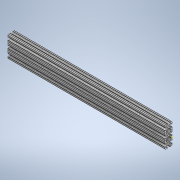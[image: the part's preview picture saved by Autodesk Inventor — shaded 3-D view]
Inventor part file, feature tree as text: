
AUTODESK INVENTOR PART (.ipt)
format: ipt  version: 2020 (Build 240168000, 168)  size: 379,904 bytes
history: native  units: in
note: dims shown in document units (in); Inventor stores cm internally (conversion verified against a paired STEP export)
features: sketch x2, extrude x1
ambient origin geometry x8: Origin, YZ Plane, XZ Plane, XY Plane, X Axis, Y Axis, Z Axis, Center Point
bodies: Solid1 (feature_tree)
feature tree (3):
  extrude  "Extrusion1"  [1 undecoded]
  sketch  "Sketch2"
  sketch  "Sketch1"  dims[d0=22.0in d1=0.0in]
note: 1 required parameter value undecoded (feature->parameter linkage not recoverable at this tier; creation-order binding heuristic only, values carry confidence <= 0.55)
